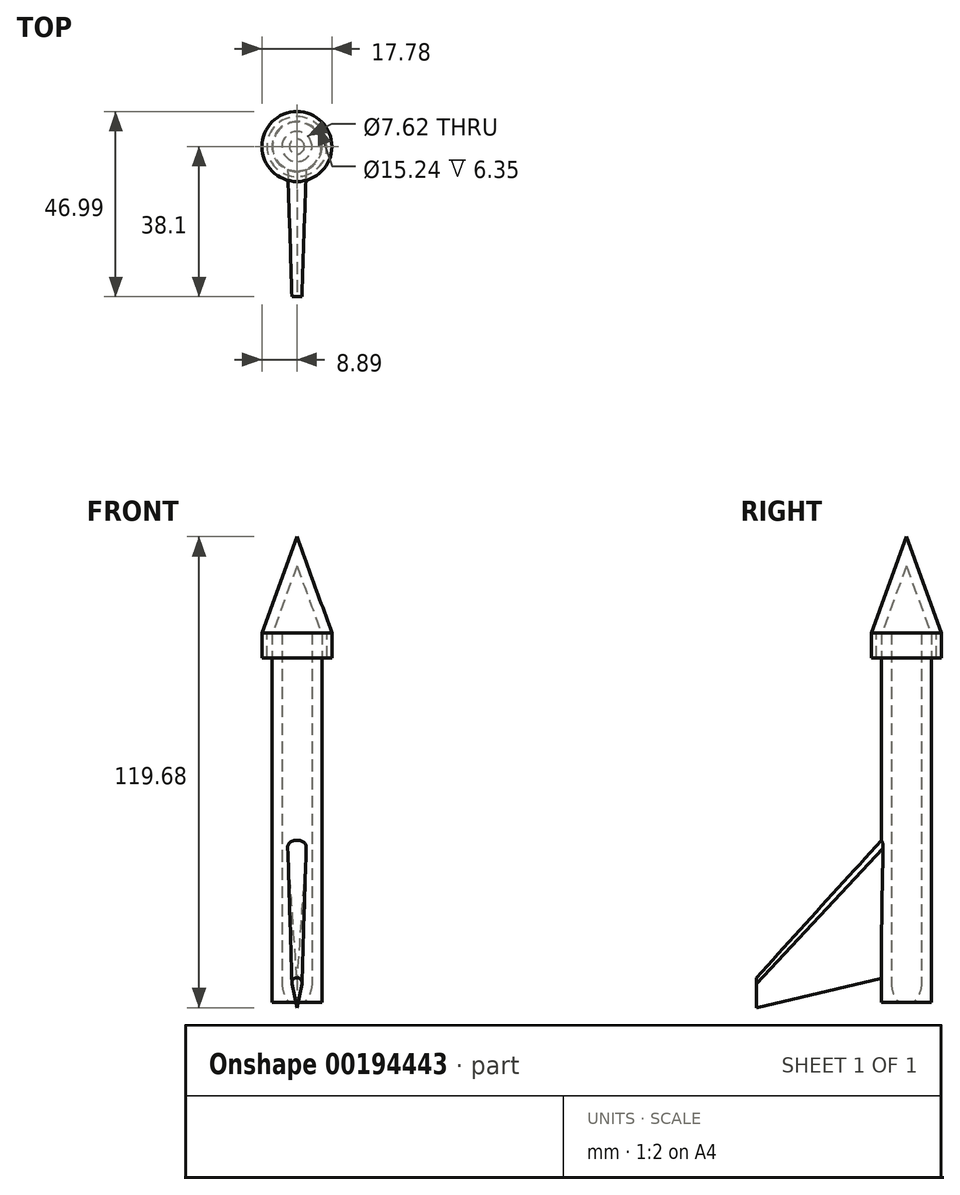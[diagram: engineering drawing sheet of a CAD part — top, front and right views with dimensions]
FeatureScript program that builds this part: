
annotation { "Feature Type Name" : "Feature", "Feature Type Description" : "" }
export const myFeature = defineFeature(function(context is Context, id is Id, definition is map)
    precondition{}
    {
        {
            var Q0;
            Q0=qCreatedBy(makeId("Top.planeOp"),FACE);
            var sketch = newSketch(context, id + "F0", { "sketchPlane" : qUnion([Q0])});
            skCircle(sketch, "E0", {"center": v(0, 0) * mm, "radius": 3.81 * mm});
            skCircle(sketch, "E1.0", {"center": v(0, 0) * mm, "radius": 6.35 * mm});
            skSolve(sketch);
        }
        {
            var Q0;
            Q0 = qSketchRegion(id + "F0", true);
            extrude(context, id + "F1", {"entities" : qUnion([Q0]), "depth" : 88.9 * mm});
        }
        {
            var Q0;
            Q0=qCreatedBy(makeId("Front.planeOp"),FACE);
            cPlane(context, id + "F2", {"entities" : qUnion([Q0]), "cplaneType" : CPlaneType.OFFSET, "offset" : 38.1 * mm, "width" : 152.4 * mm, "height" : 152.4 * mm});
        }
        {
            var Q0;
            Q0=qCreatedBy(makeId("Front.planeOp"),FACE);
            var sketch = newSketch(context, id + "F3", { "sketchPlane" : qUnion([Q0])});
            skArc(sketch, "E2", {"start": v(2.53, 40.47) * mm, "mid": v(0, 43.18) * mm, "end": v(-2.53, 40.47) * mm});
            skLineSegment(sketch, "E3", {"start": v(-2.53, 40.47) * mm, "end": v(0, 2.54) * mm});
            skLineSegment(sketch, "E4", {"start": v(0, 2.54) * mm, "end": v(2.53, 40.47) * mm});
            skSolve(sketch);
        }
        {
            var Q0;
            Q0=qCreatedBy(id+"F2.planeOp",FACE);
            var sketch = newSketch(context, id + "F4", { "sketchPlane" : qUnion([Q0])});
            skArc(sketch, "E5", {"start": v(1.24, -0.25) * mm, "mid": v(0, 1.27) * mm, "end": v(-1.24, -0.25) * mm});
            skLineSegment(sketch, "E6", {"start": v(0, -6.35) * mm, "end": v(-1.24, -0.25) * mm});
            skLineSegment(sketch, "E7", {"start": v(1.24, -0.25) * mm, "end": v(0, -6.35) * mm});
            skSolve(sketch);
        }
        {
            var Q1;
            Q1 = qSketchRegion(id + "F3", true);
            var Q2;
            Q2 = qSketchRegion(id + "F4", true);
            loft(context, id + "F5", {"operationType" : NewBodyOperationType.ADD, "sheetProfilesArray" : [{ "sheetProfileEntities" : qUnion([Q1]) }, { "sheetProfileEntities" : qUnion([Q2]) }]});
        }
        {
            var Q0;
            Q0=qCreatedBy(makeId("Top.planeOp"),FACE);
            var sketch = newSketch(context, id + "F6", { "sketchPlane" : qUnion([Q0])});
            skCircle(sketch, "E8.0", {"center": v(0, 0) * mm, "radius": 3.81 * mm});
            skSolve(sketch);
        }
        {
            var Q0;
            Q0 = qSketchRegion(id + "F6", true);
            var Q1;
            Q1=makeQuery(id+"F1.opExtrude","CAP_FACE",FACE,{"disambiguationData":[OSD([sQuery(id+"F0.wireOp",EDGE,"E0"),sQuery(id+"F0.wireOp",EDGE,"E1.0")])],"isStart":false});
            extrude(context, id + "F7", {"entities" : qUnion([Q0]), "operationType" : NewBodyOperationType.REMOVE, "endBound" : BoundingType.UP_TO_SURFACE, "endBoundEntityFace" : qUnion([Q1]), "depth" : 25.4 * mm});
        }
        {
            var Q0;
            Q0=qCreatedBy(makeId("Front.planeOp"),FACE);
            var sketch = newSketch(context, id + "F8", { "sketchPlane" : qUnion([Q0])});
            skLineSegment(sketch, "E9.0", {"start": v(-3.81, 0) * mm, "end": v(3.81, 0) * mm, "construction": true});
            skArc(sketch, "E10", {"start": v(1.9, -5.04) * mm, "mid": v(3.32, -2.7) * mm, "end": v(3.81, 0) * mm});
            skArc(sketch, "E11", {"start": v(-3.81, 0) * mm, "mid": v(-3.32, -2.7) * mm, "end": v(-1.9, -5.04) * mm, "construction": true});
            skLineSegment(sketch, "E12", {"start": v(-1.9, -5.04) * mm, "end": v(1.9, -5.04) * mm, "construction": true});
            skLineSegment(sketch, "E13", {"start": v(1.9, -5.04) * mm, "end": v(6.35, -5.04) * mm});
            skLineSegment(sketch, "E14", {"start": v(6.35, -5.04) * mm, "end": v(6.35, 0) * mm});
            skLineSegment(sketch, "E15", {"start": v(6.35, 0) * mm, "end": v(3.81, 0) * mm, "construction": true});
            skLineSegment(sketch, "E16.1", {"start": v(-6.35, 0) * mm, "end": v(6.35, 0) * mm});
            skSolve(sketch);
        }
        {
            var Q0;
            {var subQ0=sQuery(id+"F8.wireOp",EDGE,"E10");Q0=makeQuery(id+"F8.imprint","IMPRINT",FACE,{"disambiguationData":[TD([[makeQuery(id+"F8.imprint","IMPRINT",EDGE,{"derivedFrom":subQ0}),-1.0]])]});}
            var Q1;
            Q1=sQuery(id+"F8.wireOp",EDGE,"E14");
            var Q2;
            Q2=makeQuery(id+"F1.opExtrude","SWEPT_FACE",FACE,{"disambiguationData":[OSD([sQuery(id+"F0.wireOp",EDGE,"E1.0")])]});
            revolve(context, id + "F9", {"operationType" : NewBodyOperationType.ADD, "entities" : qUnion([Q0]), "surfaceEntities" : qUnion([Q1]), "axis" : qUnion([Q2]), "revolveType" : RevolveType.FULL});
        }
        {
            var Q0;
            Q0=makeQuery(id+"F1.opExtrude","CAP_FACE",FACE,{"disambiguationData":[OSD([sQuery(id+"F0.wireOp",EDGE,"E0"),sQuery(id+"F0.wireOp",EDGE,"E1.0")])],"isStart":false});
            var sketch = newSketch(context, id + "F10", { "sketchPlane" : qUnion([Q0])});
            skCircle(sketch, "E17.0", {"center": v(0, 0) * mm, "radius": 7.62 * mm});
            skCircle(sketch, "E18.0", {"center": v(0, 0) * mm, "radius": 8.9 * mm});
            skSolve(sketch);
        }
        {
            var Q0;
            Q0=makeQuery(id+"F10.imprint","IMPRINT",FACE,{"disambiguationData":[TD([[makeQuery(id+"F10.imprint","IMPRINT",EDGE,{"derivedFrom":sQuery(id+"F10.wireOp",EDGE,"E17.0")}),-1.0]])]});
            extrude(context, id + "F11", {"entities" : qUnion([Q0]), "oppositeDirection" : true, "depth" : 6.35 * mm});
        }
        {
            var Q0;
            Q0=makeQuery(id+"F11.opExtrude","CAP_FACE",FACE,{"disambiguationData":[OSD([sQuery(id+"F10.wireOp",EDGE,"E17.0"),sQuery(id+"F10.wireOp",EDGE,"E18.0")])],"isStart":true});
            var sketch = newSketch(context, id + "F12", { "sketchPlane" : qUnion([Q0])});
            skCircle(sketch, "E19.0", {"center": v(0, 0) * mm, "radius": 8.9 * mm});
            skSolve(sketch);
        }
        {
            var Q0;
            Q0 = qSketchRegion(id + "F12", true);
            extrude(context, id + "F13", {"entities" : qUnion([Q0]), "operationType" : NewBodyOperationType.ADD, "depth" : 25.4 * mm, "hasDraft" : true, "draftAngle" : 20 * degree, "draftPullDirection" : true});
        }
        {
            var Q0;
            Q0=makeQuery(id+"F13.opExtrude","CAP_FACE",FACE,{"disambiguationData":[OSD([sQuery(id+"F12.wireOp",EDGE,"E19.0")])],"isStart":true});
            shell(context, id + "F14", {"entities" : qUnion([Q0]), "thickness" : 2.54 * mm});
        }
    });
